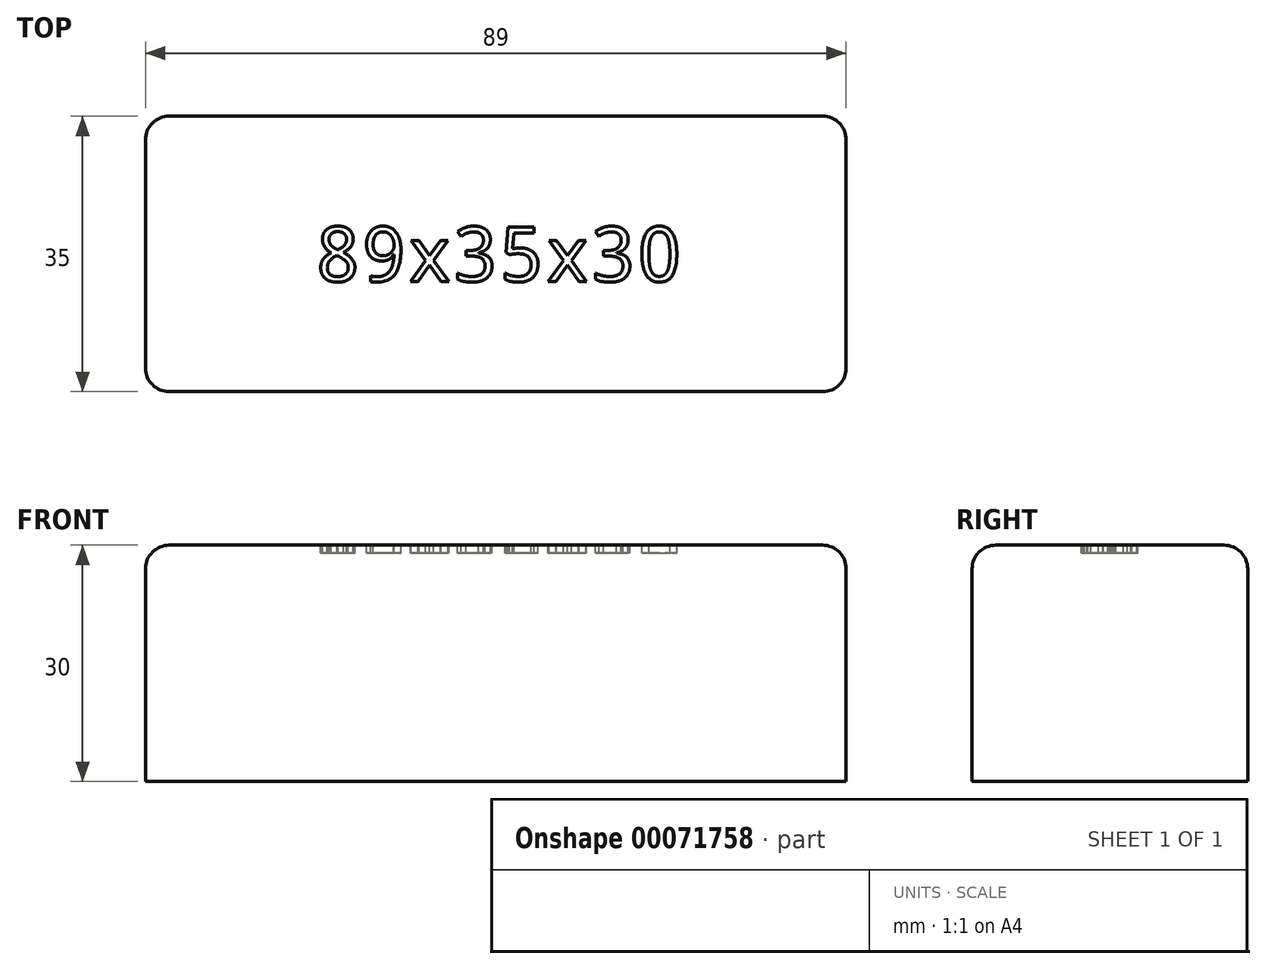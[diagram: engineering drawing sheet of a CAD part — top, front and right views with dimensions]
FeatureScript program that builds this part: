
annotation { "Feature Type Name" : "Feature", "Feature Type Description" : "" }
export const myFeature = defineFeature(function(context is Context, id is Id, definition is map)
    precondition{}
    {
        {
            var Q0;
            Q0=qCreatedBy(makeId("Top.planeOp"),FACE);
            var sketch = newSketch(context, id + "F0", { "sketchPlane" : qUnion([Q0])});
            skLineSegment(sketch, "E0.rect.bottom", {"start": v(-44.5, 17.5) * mm, "end": v(44.5, 17.5) * mm});
            skLineSegment(sketch, "E0.rect.top", {"start": v(-44.5, -17.5) * mm, "end": v(44.5, -17.5) * mm});
            skLineSegment(sketch, "E0.rect.left", {"start": v(-44.5, 17.5) * mm, "end": v(-44.5, -17.5) * mm});
            skLineSegment(sketch, "E0.rect.right", {"start": v(44.5, 17.5) * mm, "end": v(44.5, -17.5) * mm});
            skPoint(sketch, "E0.rect.middle", {"position": v(0, 0) * mm});
            skSolve(sketch);
        }
        {
            var Q0;
            Q0 = qSketchRegion(id + "F0", true);
            extrude(context, id + "F1", {"entities" : qUnion([Q0]), "endBound" : BoundingType.SYMMETRIC, "depth" : 30 * mm});
        }
        {
            var Q0;
            Q0=makeQuery(id+"F1.opExtrude","CAP_FACE",FACE,{"disambiguationData":[OSD([sQuery(id+"F0.wireOp",EDGE,"E0.rect.bottom"),sQuery(id+"F0.wireOp",EDGE,"E0.rect.top"),sQuery(id+"F0.wireOp",EDGE,"E0.rect.left"),sQuery(id+"F0.wireOp",EDGE,"E0.rect.right")])],"isStart":false});
            var Q1;
            Q1=makeQuery(id+"F1.opExtrude","SWEPT_EDGE",EDGE,{"disambiguationData":[OSD([sQuery(id+"F0.wireOp",EDGE,"E0.rect.bottom"),sQuery(id+"F0.wireOp",EDGE,"E0.rect.right")])]});
            var Q2;
            Q2=makeQuery(id+"F1.opExtrude","SWEPT_EDGE",EDGE,{"disambiguationData":[OSD([sQuery(id+"F0.wireOp",EDGE,"E0.rect.top"),sQuery(id+"F0.wireOp",EDGE,"E0.rect.right")])]});
            var Q3;
            Q3=makeQuery(id+"F1.opExtrude","SWEPT_EDGE",EDGE,{"disambiguationData":[OSD([sQuery(id+"F0.wireOp",EDGE,"E0.rect.top"),sQuery(id+"F0.wireOp",EDGE,"E0.rect.left")])]});
            var Q4;
            Q4=makeQuery(id+"F1.opExtrude","SWEPT_EDGE",EDGE,{"disambiguationData":[OSD([sQuery(id+"F0.wireOp",EDGE,"E0.rect.bottom"),sQuery(id+"F0.wireOp",EDGE,"E0.rect.left")])]});
            fillet(context, id + "F2", {"entities" : qUnion([Q0, Q1, Q2, Q3, Q4]), "radius" : 3 * mm, "tangentPropagation" : true, "allowEdgeOverflow" : false});
        }
        {
            var Q0;
            Q0=makeQuery(id+"F1.opExtrude","CAP_FACE",FACE,{"disambiguationData":[OSD([sQuery(id+"F0.wireOp",EDGE,"E0.rect.bottom"),sQuery(id+"F0.wireOp",EDGE,"E0.rect.top"),sQuery(id+"F0.wireOp",EDGE,"E0.rect.left"),sQuery(id+"F0.wireOp",EDGE,"E0.rect.right")])],"isStart":false});
            var sketch = newSketch(context, id + "F3", { "sketchPlane" : qUnion([Q0])});
            skText(sketch, "E1", { "text": "89x35x30", "fontName": "DroidSansMono.ttf"});
            const initialGuessF3  = {"E1": [-0.02299, -0.0035, 1, 0, 0.007]};
            skSetInitialGuess(sketch, initialGuessF3);
            skSolve(sketch);
        }
        {
            var Q0;
            Q0 = qSketchRegion(id + "F3", true);
            extrude(context, id + "F4", {"entities" : qUnion([Q0]), "operationType" : NewBodyOperationType.REMOVE, "oppositeDirection" : true, "depth" : 1 * mm});
        }
    });
